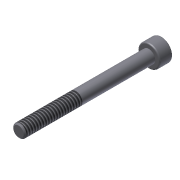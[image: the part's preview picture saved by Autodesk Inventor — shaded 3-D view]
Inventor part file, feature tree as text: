
AUTODESK INVENTOR PART (.ipt)
format: ipt  version: 2011 SP1 (Build 150282100, 282)  size: 105,472 bytes
history: native  units: in
note: dims shown in document units (in); Inventor stores cm internally (conversion verified against a paired STEP export)
features: extrude x3, sketch x3, thread x1, chamfer x1, fillet x1
ambient origin geometry x8: Origin, YZ Plane, XZ Plane, XY Plane, X Axis, Y Axis, Z Axis, Center Point
bodies: Solid1 (feature_tree)
feature tree (9):
  extrude  "Extrusion1"  Depth=1.9685in TaperAngle=0.0deg
  extrude  "Extrusion2"  Depth=0.1969in TaperAngle=0.0deg
  extrude  "Extrusion3"  Depth=0.0984in TaperAngle=0.0deg
  thread  "Thread1"  [1 undecoded]
  chamfer  "Chamfer1"  Distance=0.02in Angle=45.0deg
  fillet  "Fillet1"  Radius=0.02in
  sketch  "Sketch1"  dims[d0=0.1969in d1=1.9685in d2=0.0in]
  sketch  "Sketch2"  dims[d3=0.3346in d4=0.1969in d5=0.0in]
  sketch  "Sketch3"  dims[d6=0.1575in d7=0.0984in d8=0.0in d9=0.8661in d10=0.0in d11=0.02in d12=0.125in d13=45.0deg d14=0.02in]
note: 1 required parameter value undecoded (feature->parameter linkage not recoverable at this tier; creation-order binding heuristic only, values carry confidence <= 0.55)
